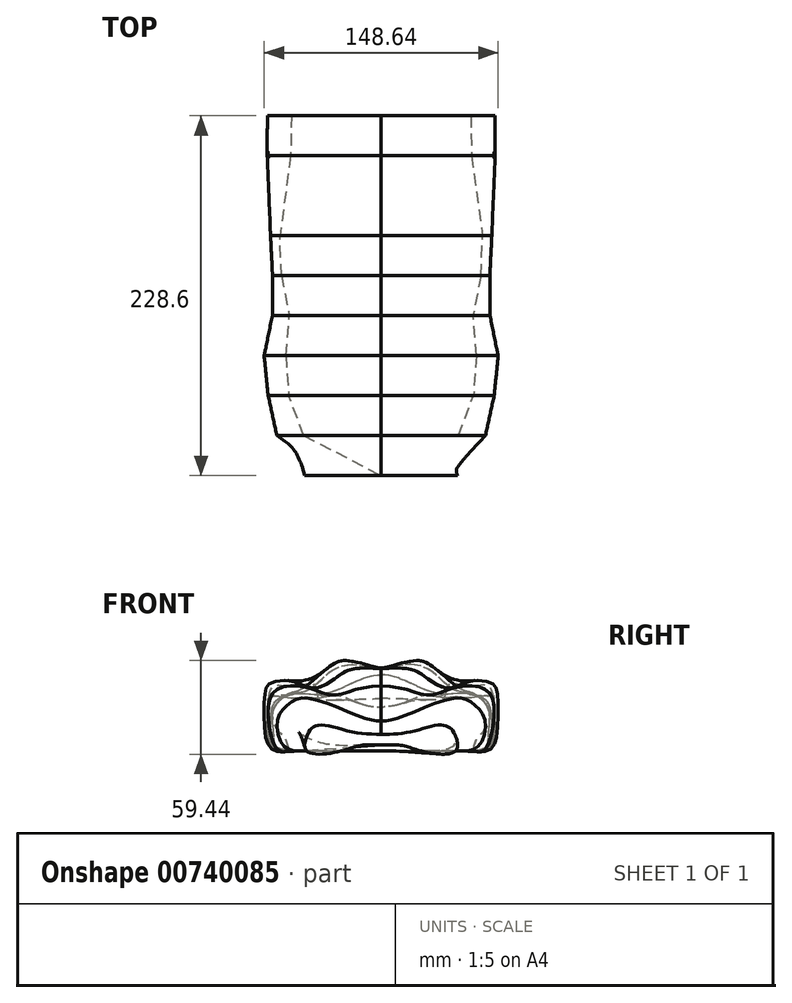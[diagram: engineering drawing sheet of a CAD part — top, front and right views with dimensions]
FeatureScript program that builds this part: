
annotation { "Feature Type Name" : "Feature", "Feature Type Description" : "" }
export const myFeature = defineFeature(function(context is Context, id is Id, definition is map)
    precondition{}
    {
        {
            var Q0;
            Q0=qCreatedBy(makeId("Front.planeOp"),FACE);
            var sketch = newSketch(context, id + "F0", { "sketchPlane" : qUnion([Q0])});
            skFitSpline(sketch, "E0", {"points": [v(-57, 0) * mm, v(-70.38, 5.16) * mm, v(-71.93, 28.23) * mm, v(-69.98, 39.02) * mm, v(-67.02, 41.48) * mm, v(-60.16, 41.22) * mm, v(-50.36, 41.47) * mm, v(-45.46, 42.94) * mm, v(-42.51, 41.47) * mm, v(-40.32, 34.6) * mm, v(-38.1, 32.64) * mm, v(-23.65, 32.4) * mm, v(0, 33.13) * mm], "startDerivative": vector(-236.05, 0) * mm, "endDerivative": vector(119.48, 0) * mm});
            skFitSpline(sketch, "E1.MirrorCS", {"points": [v(57, 0) * mm, v(70.38, 5.16) * mm, v(71.93, 28.23) * mm, v(69.98, 39.02) * mm, v(67.02, 41.48) * mm, v(60.16, 41.22) * mm, v(50.36, 41.47) * mm, v(45.46, 42.94) * mm, v(42.51, 41.47) * mm, v(40.32, 34.6) * mm, v(38.1, 32.64) * mm, v(23.65, 32.4) * mm, v(0, 33.13) * mm], "startDerivative": vector(236.05, 0) * mm, "endDerivative": vector(-119.48, 0) * mm});
            skLineSegment(sketch, "E2", {"start": v(-57, 0) * mm, "end": v(57, 0) * mm});
            skSolve(sketch);
        }
        {
            var Q0;
            Q0=makeQuery(id+"F0.imprint","IMPRINT",FACE,{"disambiguationData":[TD([[makeQuery(id+"F0.imprint","IMPRINT",EDGE,{"derivedFrom":sQuery(id+"F0.wireOp",EDGE,"E0")}),-1.0]])]});
            cPlane(context, id + "F1", {"entities" : qUnion([Q0]), "cplaneType" : CPlaneType.OFFSET, "offset" : 0 * mm, "width" : 152.4 * mm, "height" : 152.4 * mm});
        }
        {
            var Q0;
            Q0=qCreatedBy(id+"F1.planeOp",FACE);
            cPlane(context, id + "F2", {"entities" : qUnion([Q0]), "cplaneType" : CPlaneType.OFFSET, "offset" : 25.4 * mm, "width" : 152.4 * mm, "height" : 152.4 * mm});
        }
        {
            var Q0;
            Q0=qCreatedBy(id+"F2.planeOp",FACE);
            cPlane(context, id + "F3", {"entities" : qUnion([Q0]), "cplaneType" : CPlaneType.OFFSET, "offset" : 25.4 * mm, "width" : 152.4 * mm, "height" : 152.4 * mm});
        }
        {
            var Q0;
            Q0=qCreatedBy(id+"F3.planeOp",FACE);
            cPlane(context, id + "F4", {"entities" : qUnion([Q0]), "cplaneType" : CPlaneType.OFFSET, "offset" : 25.4 * mm, "width" : 152.4 * mm, "height" : 152.4 * mm});
        }
        {
            var Q0;
            Q0=qCreatedBy(id+"F4.planeOp",FACE);
            cPlane(context, id + "F5", {"entities" : qUnion([Q0]), "cplaneType" : CPlaneType.OFFSET, "offset" : 25.4 * mm, "width" : 152.4 * mm, "height" : 152.4 * mm});
        }
        {
            var Q0;
            Q0=qCreatedBy(id+"F5.planeOp",FACE);
            cPlane(context, id + "F6", {"entities" : qUnion([Q0]), "cplaneType" : CPlaneType.OFFSET, "offset" : 25.4 * mm, "width" : 152.4 * mm, "height" : 152.4 * mm});
        }
        {
            var Q0;
            Q0=qCreatedBy(id+"F6.planeOp",FACE);
            cPlane(context, id + "F7", {"entities" : qUnion([Q0]), "cplaneType" : CPlaneType.OFFSET, "offset" : 25.4 * mm, "width" : 152.4 * mm, "height" : 152.4 * mm});
        }
        {
            var Q0;
            Q0=qCreatedBy(id+"F7.planeOp",FACE);
            cPlane(context, id + "F8", {"entities" : qUnion([Q0]), "cplaneType" : CPlaneType.OFFSET, "offset" : 25.4 * mm, "width" : 152.4 * mm, "height" : 152.4 * mm});
        }
        {
            var Q0;
            Q0=qCreatedBy(id+"F8.planeOp",FACE);
            cPlane(context, id + "F9", {"entities" : qUnion([Q0]), "cplaneType" : CPlaneType.OFFSET, "offset" : 25.4 * mm, "width" : 152.4 * mm, "height" : 152.4 * mm});
        }
        {
            var Q0;
            Q0=qCreatedBy(id+"F9.planeOp",FACE);
            cPlane(context, id + "F10", {"entities" : qUnion([Q0]), "cplaneType" : CPlaneType.OFFSET, "offset" : 25.4 * mm, "width" : 152.4 * mm, "height" : 152.4 * mm});
        }
        {
            var Q0;
            Q0=qCreatedBy(id+"F2.planeOp",FACE);
            var sketch = newSketch(context, id + "F11", { "sketchPlane" : qUnion([Q0])});
            skLineSegment(sketch, "E3", {"start": v(0, 0) * mm, "end": v(-57.48, 0) * mm});
            skFitSpline(sketch, "E4", {"points": [v(-57.48, 0) * mm, v(-70.55, 4.97) * mm, v(-71.74, 28.73) * mm, v(-71.14, 34.08) * mm, v(-65.5, 34.67) * mm, v(-54.5, 33.48) * mm, v(-46.79, 34.08) * mm, v(-39.66, 33.48) * mm, v(-28.96, 35.27) * mm, v(-13.22, 29.92) * mm, v(0, 27.54) * mm], "startDerivative": vector(-141.77, 9.84) * mm, "endDerivative": vector(116.24, -10.5) * mm});
            skFitSpline(sketch, "E5.MirrorCS", {"points": [v(57.48, 0) * mm, v(70.55, 4.97) * mm, v(71.74, 28.73) * mm, v(71.14, 34.08) * mm, v(65.5, 34.67) * mm, v(54.5, 33.48) * mm, v(46.79, 34.08) * mm, v(39.66, 33.48) * mm, v(28.96, 35.27) * mm, v(13.22, 29.92) * mm, v(0, 27.54) * mm], "startDerivative": vector(141.77, 9.84) * mm, "endDerivative": vector(-116.24, -10.5) * mm});
            skLineSegment(sketch, "E6.MirrorCS", {"start": v(0, 0) * mm, "end": v(57.48, 0) * mm});
            skSolve(sketch);
        }
        {
            var Q0;
            Q0=qCreatedBy(id+"F4.planeOp",FACE);
            var sketch = newSketch(context, id + "F12", { "sketchPlane" : qUnion([Q0])});
            skLineSegment(sketch, "E7", {"start": v(0, 0) * mm, "end": v(-64.31, 0) * mm});
            skFitSpline(sketch, "E8", {"points": [v(-64.31, 0) * mm, v(-68.77, 3.78) * mm, v(-70.25, 12.7) * mm, v(-68.17, 29.92) * mm, v(-61.04, 34.67) * mm, v(-50.94, 36.45) * mm, v(-39.36, 35.86) * mm, v(-24.2, 40.32) * mm, v(-9.65, 46.55) * mm, v(0, 48.34) * mm], "startDerivative": vector(-64.65, 40.28) * mm, "endDerivative": vector(89.44, 9.95) * mm});
            skFitSpline(sketch, "E9.MirrorCS", {"points": [v(64.31, 0) * mm, v(68.77, 3.78) * mm, v(70.25, 12.7) * mm, v(68.17, 29.92) * mm, v(61.04, 34.67) * mm, v(50.94, 36.45) * mm, v(39.36, 35.86) * mm, v(24.2, 40.32) * mm, v(9.65, 46.55) * mm, v(0, 48.34) * mm], "startDerivative": vector(64.65, 40.28) * mm, "endDerivative": vector(-89.44, 9.95) * mm});
            skLineSegment(sketch, "E10.MirrorCS", {"start": v(0, 0) * mm, "end": v(64.31, 0) * mm});
            skSolve(sketch);
        }
        {
            var Q0;
            Q0=qCreatedBy(id+"F5.planeOp",FACE);
            var sketch = newSketch(context, id + "F13", { "sketchPlane" : qUnion([Q0])});
            skLineSegment(sketch, "E11", {"start": v(0, 0) * mm, "end": v(-63.42, 0) * mm});
            skFitSpline(sketch, "E12", {"points": [v(-63.42, 0) * mm, v(-66.69, 0) * mm, v(-68.17, 10.31) * mm, v(-68.17, 26.35) * mm, v(-58.67, 35.86) * mm, v(-47.38, 38.24) * mm, v(-36.98, 46.26) * mm, v(-27.18, 53.09) * mm, v(-15.9, 54.57) * mm, v(-5.2, 52.2) * mm, v(0, 51.9) * mm], "startDerivative": vector(-66.85, -18.43) * mm, "endDerivative": vector(66.92, 1.52) * mm});
            skLineSegment(sketch, "E13.MirrorCS", {"start": v(0, 0) * mm, "end": v(63.42, 0) * mm});
            skFitSpline(sketch, "E14.MirrorCS", {"points": [v(63.42, 0) * mm, v(66.69, 0) * mm, v(68.17, 10.31) * mm, v(68.17, 26.35) * mm, v(58.67, 35.86) * mm, v(47.38, 38.24) * mm, v(36.98, 46.26) * mm, v(27.18, 53.09) * mm, v(15.9, 54.57) * mm, v(5.2, 52.2) * mm, v(0, 51.9) * mm], "startDerivative": vector(66.85, -18.43) * mm, "endDerivative": vector(-66.92, 1.52) * mm});
            skSolve(sketch);
        }
        {
            var Q0;
            Q0=qCreatedBy(id+"F6.planeOp",FACE);
            var sketch = newSketch(context, id + "F14", { "sketchPlane" : qUnion([Q0])});
            skLineSegment(sketch, "E15", {"start": v(0, 0) * mm, "end": v(-58.37, 0) * mm});
            skFitSpline(sketch, "E16", {"points": [v(-58.37, 0) * mm, v(-61.04, 7.94) * mm, v(-65.8, 13.28) * mm, v(-68.77, 25.17) * mm, v(-58.37, 36.45) * mm, v(-51.24, 38.83) * mm, v(-39.06, 48.34) * mm, v(-29.56, 55.47) * mm, v(-23.02, 57.25) * mm, v(-12.33, 55.47) * mm, v(-5.2, 53.39) * mm, v(0, 52.5) * mm], "startDerivative": vector(-23.4, 103.21) * mm, "endDerivative": vector(75.83, -10.2) * mm});
            skFitSpline(sketch, "E17.MirrorCS", {"points": [v(58.37, 0) * mm, v(61.04, 7.94) * mm, v(65.8, 13.28) * mm, v(68.77, 25.17) * mm, v(58.37, 36.45) * mm, v(51.24, 38.83) * mm, v(39.06, 48.34) * mm, v(29.56, 55.47) * mm, v(23.02, 57.25) * mm, v(12.33, 55.47) * mm, v(5.2, 53.39) * mm, v(0, 52.5) * mm], "startDerivative": vector(23.4, 103.21) * mm, "endDerivative": vector(-75.83, -10.2) * mm});
            skLineSegment(sketch, "E18.MirrorCS", {"start": v(0, 0) * mm, "end": v(58.37, 0) * mm});
            skSolve(sketch);
        }
        {
            var Q0;
            Q0=qCreatedBy(id+"F7.planeOp",FACE);
            var sketch = newSketch(context, id + "F15", { "sketchPlane" : qUnion([Q0])});
            skLineSegment(sketch, "E19", {"start": v(0, 0) * mm, "end": v(-60.45, 0) * mm});
            skFitSpline(sketch, "E20", {"points": [v(-60.45, 0) * mm, v(-67.88, 0) * mm, v(-71.74, 3.78) * mm, v(-73.82, 12.7) * mm, v(-74.11, 33.48) * mm, v(-72.93, 40.02) * mm, v(-70.55, 42.7) * mm, v(-60.45, 44.77) * mm, v(-50.35, 41.8) * mm, v(-40.84, 40.02) * mm, v(-28.37, 46.55) * mm, v(-20.64, 51.3) * mm, v(-9.65, 52.5) * mm, v(0, 52.2) * mm], "startDerivative": vector(-118.45, -16.28) * mm, "endDerivative": vector(119.05, -5.53) * mm});
            skLineSegment(sketch, "E21.MirrorCS", {"start": v(0, 0) * mm, "end": v(60.45, 0) * mm});
            skFitSpline(sketch, "E22.MirrorCS", {"points": [v(60.45, 0) * mm, v(67.88, 0) * mm, v(71.74, 3.78) * mm, v(73.82, 12.7) * mm, v(74.11, 33.48) * mm, v(72.93, 40.02) * mm, v(70.55, 42.7) * mm, v(60.45, 44.77) * mm, v(50.35, 41.8) * mm, v(40.84, 40.02) * mm, v(28.37, 46.55) * mm, v(20.64, 51.3) * mm, v(9.65, 52.5) * mm, v(0, 52.2) * mm], "startDerivative": vector(118.45, -16.28) * mm, "endDerivative": vector(-119.05, -5.53) * mm});
            skSolve(sketch);
        }
        {
            var Q0;
            Q0=qCreatedBy(id+"F8.planeOp",FACE);
            var sketch = newSketch(context, id + "F16", { "sketchPlane" : qUnion([Q0])});
            skLineSegment(sketch, "E23", {"start": v(0, 0) * mm, "end": v(-58.67, 0) * mm});
            skFitSpline(sketch, "E24", {"points": [v(-58.67, 0) * mm, v(-65.2, 0) * mm, v(-70.55, 12.7) * mm, v(-71.44, 29.92) * mm, v(-67.88, 37.64) * mm, v(-58.67, 41.2) * mm, v(-44.4, 39.42) * mm, v(-34.3, 35.86) * mm, v(-25.4, 35.86) * mm, v(-15.3, 39.13) * mm, v(0, 41.2) * mm], "startDerivative": vector(-92.78, -23.35) * mm, "endDerivative": vector(138.83, 11.25) * mm});
            skLineSegment(sketch, "E25.MirrorCS", {"start": v(0, 0) * mm, "end": v(58.67, 0) * mm});
            skFitSpline(sketch, "E26.MirrorCS", {"points": [v(58.67, 0) * mm, v(65.2, 0) * mm, v(70.55, 12.7) * mm, v(71.44, 29.92) * mm, v(67.88, 37.64) * mm, v(58.67, 41.2) * mm, v(44.4, 39.42) * mm, v(34.3, 35.86) * mm, v(25.4, 35.86) * mm, v(15.3, 39.13) * mm, v(0, 41.2) * mm], "startDerivative": vector(92.78, -23.35) * mm, "endDerivative": vector(-138.83, 11.25) * mm});
            skSolve(sketch);
        }
        {
            var Q0;
            Q0=qCreatedBy(id+"F9.planeOp",FACE);
            var sketch = newSketch(context, id + "F17", { "sketchPlane" : qUnion([Q0])});
            skLineSegment(sketch, "E27", {"start": v(0, 0) * mm, "end": v(-49.16, 0) * mm});
            skFitSpline(sketch, "E28", {"points": [v(-49.16, 0) * mm, v(-61.64, 2.6) * mm, v(-65.8, 19.82) * mm, v(-58.67, 29.62) * mm, v(-46.79, 33.48) * mm, v(-11.73, 21) * mm, v(0, 18.93) * mm], "startDerivative": vector(-95.25, -4.54) * mm, "endDerivative": vector(67.62, -2.94) * mm});
            skLineSegment(sketch, "E29.MirrorCS", {"start": v(0, 0) * mm, "end": v(49.16, 0) * mm});
            skFitSpline(sketch, "E30.MirrorCS", {"points": [v(49.16, 0) * mm, v(61.64, 2.6) * mm, v(65.8, 19.82) * mm, v(58.67, 29.62) * mm, v(46.79, 33.48) * mm, v(11.73, 21) * mm, v(0, 18.93) * mm], "startDerivative": vector(95.25, -4.54) * mm, "endDerivative": vector(-67.62, -2.94) * mm});
            skSolve(sketch);
        }
        {
            var Q0;
            Q0=qCreatedBy(id+"F10.planeOp",FACE);
            var sketch = newSketch(context, id + "F18", { "sketchPlane" : qUnion([Q0])});
            skFitSpline(sketch, "E31", {"points": [v(0, 3.78) * mm, v(-14.1, 3.19) * mm, v(-24.8, 0) * mm, v(-47.38, 0) * mm, v(-46.2, 11.5) * mm, v(-42.92, 15.07) * mm, v(-36.1, 16.26) * mm, v(-19.16, 12.1) * mm, v(0, 10.31) * mm], "startDerivative": vector(-117.53, 1.37) * mm, "endDerivative": vector(124.67, -3.68) * mm});
            skFitSpline(sketch, "E32.MirrorCS", {"points": [v(0, 3.78) * mm, v(14.1, 3.19) * mm, v(24.8, 0) * mm, v(47.38, 0) * mm, v(46.2, 11.5) * mm, v(42.92, 15.07) * mm, v(36.1, 16.26) * mm, v(19.16, 12.1) * mm, v(0, 10.31) * mm], "startDerivative": vector(117.53, 1.37) * mm, "endDerivative": vector(-124.67, -3.68) * mm});
            skSolve(sketch);
        }
        {
            var Q0;
            Q0=makeQuery(id+"F0.imprint","IMPRINT",FACE,{"disambiguationData":[TD([[makeQuery(id+"F0.imprint","IMPRINT",EDGE,{"derivedFrom":sQuery(id+"F0.wireOp",EDGE,"E0")}),-1.0]])]});
            var Q1;
            Q1=makeQuery(id+"F11.imprint","IMPRINT",FACE,{"disambiguationData":[TD([[makeQuery(id+"F11.imprint","IMPRINT",EDGE,{"derivedFrom":sQuery(id+"F11.wireOp",EDGE,"E3")}),-1.0]])]});
            loft(context, id + "F19", {"sheetProfilesArray" : [{ "sheetProfileEntities" : qUnion([Q0]) }, { "sheetProfileEntities" : qUnion([Q1]) }]});
        }
        {
            var Q0;
            Q0=makeQuery(id+"F17.imprint","IMPRINT",FACE,{"disambiguationData":[TD([[makeQuery(id+"F17.imprint","IMPRINT",EDGE,{"derivedFrom":sQuery(id+"F17.wireOp",EDGE,"E27")}),-1.0]])]});
            var Q1;
            Q1=makeQuery(id+"F16.imprint","IMPRINT",FACE,{"disambiguationData":[TD([[makeQuery(id+"F16.imprint","IMPRINT",EDGE,{"derivedFrom":sQuery(id+"F16.wireOp",EDGE,"E23")}),-1.0]])]});
            loft(context, id + "F20", {"sheetProfilesArray" : [{ "sheetProfileEntities" : qUnion([Q0]) }, { "sheetProfileEntities" : qUnion([Q1]) }]});
        }
        {
            var Q0;
            Q0=makeQuery(id+"F15.imprint","IMPRINT",FACE,{"disambiguationData":[TD([[makeQuery(id+"F15.imprint","IMPRINT",EDGE,{"derivedFrom":sQuery(id+"F15.wireOp",EDGE,"E19")}),-1.0]])]});
            var Q1;
            Q1=makeQuery(id+"F14.imprint","IMPRINT",FACE,{"disambiguationData":[TD([[makeQuery(id+"F14.imprint","IMPRINT",EDGE,{"derivedFrom":sQuery(id+"F14.wireOp",EDGE,"E15")}),-1.0]])]});
            loft(context, id + "F21", {"sheetProfilesArray" : [{ "sheetProfileEntities" : qUnion([Q0]) }, { "sheetProfileEntities" : qUnion([Q1]) }]});
        }
        {
            var Q0;
            Q0=makeQuery(id+"F21.opLoft","CAP_FACE",FACE,{"disambiguationData":[OSD([makeQuery(id+"F15.imprint","IMPRINT",FACE,{"disambiguationData":[TD([[makeQuery(id+"F15.imprint","IMPRINT",EDGE,{"derivedFrom":sQuery(id+"F15.wireOp",EDGE,"E19")}),-1.0]])]})])],"isStart":true});
            var Q1;
            Q1=makeQuery(id+"F20.opLoft","CAP_FACE",FACE,{"disambiguationData":[OSD([makeQuery(id+"F16.imprint","IMPRINT",FACE,{"disambiguationData":[TD([[makeQuery(id+"F16.imprint","IMPRINT",EDGE,{"derivedFrom":sQuery(id+"F16.wireOp",EDGE,"E23")}),-1.0]])]})])],"isStart":true});
            loft(context, id + "F22", {"sheetProfilesArray" : [{ "sheetProfileEntities" : qUnion([Q0]) }, { "sheetProfileEntities" : qUnion([Q1]) }]});
        }
        {
            var Q0;
            Q0=makeQuery(id+"F13.imprint","IMPRINT",FACE,{"disambiguationData":[TD([[makeQuery(id+"F13.imprint","IMPRINT",EDGE,{"derivedFrom":sQuery(id+"F13.wireOp",EDGE,"E11")}),-1.0]])]});
            var Q1;
            Q1=makeQuery(id+"F12.imprint","IMPRINT",FACE,{"disambiguationData":[TD([[makeQuery(id+"F12.imprint","IMPRINT",EDGE,{"derivedFrom":sQuery(id+"F12.wireOp",EDGE,"E7")}),-1.0]])]});
            loft(context, id + "F23", {"sheetProfilesArray" : [{ "sheetProfileEntities" : qUnion([Q0]) }, { "sheetProfileEntities" : qUnion([Q1]) }]});
        }
        {
            var Q1;
            Q1=makeQuery(id+"F20.opLoft","CAP_FACE",FACE,{"disambiguationData":[OSD([makeQuery(id+"F17.imprint","IMPRINT",FACE,{"disambiguationData":[TD([[makeQuery(id+"F17.imprint","IMPRINT",EDGE,{"derivedFrom":sQuery(id+"F17.wireOp",EDGE,"E27")}),-1.0]])]})])],"isStart":true});
            var Q2;
            Q2=makeQuery(id+"F18.imprint","IMPRINT",FACE,{"disambiguationData":[TD([[makeQuery(id+"F18.imprint","IMPRINT",EDGE,{"derivedFrom":sQuery(id+"F18.wireOp",EDGE,"E31")}),-1.0]])]});
            loft(context, id + "F24", {"operationType" : NewBodyOperationType.ADD, "sheetProfilesArray" : [{ "sheetProfileEntities" : qUnion([Q1]) }, { "sheetProfileEntities" : qUnion([Q2]) }]});
        }
        {
            var Q0;
            Q0=makeQuery(id+"F23.opLoft","CAP_FACE",FACE,{"disambiguationData":[OSD([makeQuery(id+"F13.imprint","IMPRINT",FACE,{"disambiguationData":[TD([[makeQuery(id+"F13.imprint","IMPRINT",EDGE,{"derivedFrom":sQuery(id+"F13.wireOp",EDGE,"E11")}),-1.0]])]})])],"isStart":true});
            var Q1;
            Q1=makeQuery(id+"F21.opLoft","CAP_FACE",FACE,{"disambiguationData":[OSD([makeQuery(id+"F14.imprint","IMPRINT",FACE,{"disambiguationData":[TD([[makeQuery(id+"F14.imprint","IMPRINT",EDGE,{"derivedFrom":sQuery(id+"F14.wireOp",EDGE,"E15")}),-1.0]])]})])],"isStart":true});
            loft(context, id + "F25", {"sheetProfilesArray" : [{ "sheetProfileEntities" : qUnion([Q0]) }, { "sheetProfileEntities" : qUnion([Q1]) }]});
        }
        {
            var Q0;
            Q0=makeQuery(id+"F19.opLoft","CAP_FACE",FACE,{"disambiguationData":[OSD([makeQuery(id+"F11.imprint","IMPRINT",FACE,{"disambiguationData":[TD([[makeQuery(id+"F11.imprint","IMPRINT",EDGE,{"derivedFrom":sQuery(id+"F11.wireOp",EDGE,"E3")}),-1.0]])]})])],"isStart":true});
            var Q1;
            Q1=makeQuery(id+"F23.opLoft","CAP_FACE",FACE,{"disambiguationData":[OSD([makeQuery(id+"F12.imprint","IMPRINT",FACE,{"disambiguationData":[TD([[makeQuery(id+"F12.imprint","IMPRINT",EDGE,{"derivedFrom":sQuery(id+"F12.wireOp",EDGE,"E7")}),-1.0]])]})])],"isStart":true});
            loft(context, id + "F26", {"sheetProfilesArray" : [{ "sheetProfileEntities" : qUnion([Q0]) }, { "sheetProfileEntities" : qUnion([Q1]) }]});
        }
    });
